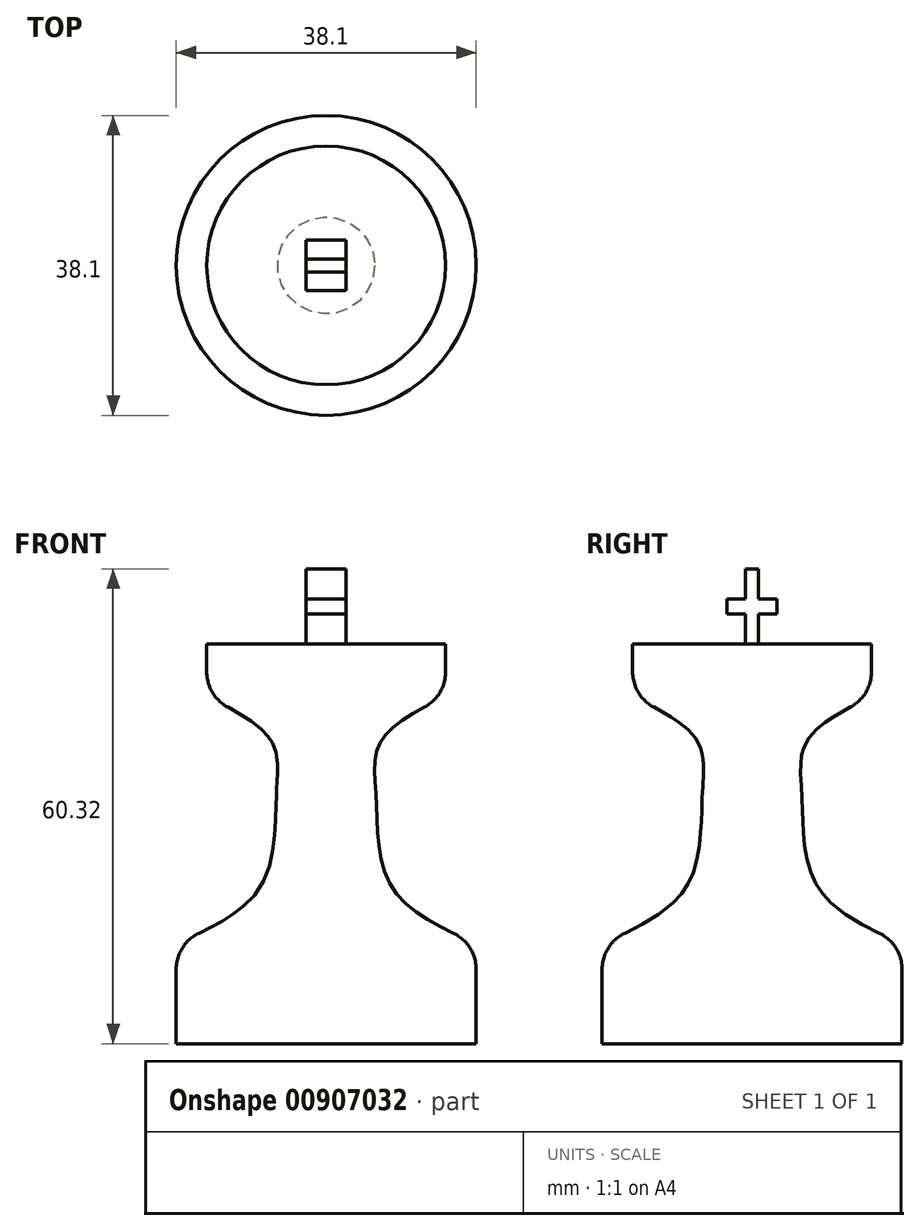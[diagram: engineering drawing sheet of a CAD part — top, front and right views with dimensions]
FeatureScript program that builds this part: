
annotation { "Feature Type Name" : "Feature", "Feature Type Description" : "" }
export const myFeature = defineFeature(function(context is Context, id is Id, definition is map)
    precondition{}
    {
        {
            var Q0;
            Q0=qCreatedBy(makeId("Front.planeOp"),FACE);
            var sketch = newSketch(context, id + "F0", { "sketchPlane" : qUnion([Q0])});
            skLineSegment(sketch, "E0", {"start": v(0, 50.8) * mm, "end": v(0, 0) * mm, "construction": true});
            skLineSegment(sketch, "E1", {"start": v(0, 0) * mm, "end": v(19.05, 0) * mm});
            skLineSegment(sketch, "E2", {"start": v(19.05, 0) * mm, "end": v(19.05, 12.7) * mm});
            skFitSpline(sketch, "E3", {"points": [v(19.05, 12.7) * mm, v(8.22, 20.12) * mm, v(6.33, 31.5) * mm, v(6.96, 38.44) * mm, v(15.17, 44.12) * mm], "startDerivative": vector(-46.7, 21.07) * mm, "endDerivative": vector(41.83, 20.88) * mm});
            skLineSegment(sketch, "E4", {"start": v(15.17, 44.12) * mm, "end": v(15.17, 50.8) * mm});
            skLineSegment(sketch, "E5", {"start": v(15.17, 50.8) * mm, "end": v(0, 50.8) * mm});
            skLineSegment(sketch, "E6", {"start": v(0, 50.8) * mm, "end": v(0, 0) * mm});
            skSolve(sketch);
        }
        {
            var Q0;
            Q0 = qSketchRegion(id + "F0", true);
            var Q1;
            Q1=sQuery(id+"F0.wireOp",EDGE,"E6");
            revolve(context, id + "F1", {"surfaceOperationType" : NewSurfaceOperationType.NEW, "entities" : qUnion([Q0]), "axis" : qUnion([Q1]), "revolveType" : RevolveType.FULL});
        }
        {
            var Q0;
            Q0=makeQuery(id+"F1.opRevolve","SWEPT_EDGE",EDGE,{"disambiguationData":[OSD([sQuery(id+"F0.wireOp",EDGE,"E2"),sQuery(id+"F0.wireOp",EDGE,"E3")])]});
            var Q1;
            Q1=makeQuery(id+"F1.opRevolve","SWEPT_EDGE",EDGE,{"disambiguationData":[OSD([sQuery(id+"F0.wireOp",EDGE,"E3"),sQuery(id+"F0.wireOp",EDGE,"E4")])]});
            fillet(context, id + "F2", {"entities" : qUnion([Q0, Q1]), "radius" : 5.08 * mm, "tangentPropagation" : true, "allowEdgeOverflow" : false});
        }
        {
            var Q0;
            Q0=qCreatedBy(makeId("Right.planeOp"),FACE);
            var sketch = newSketch(context, id + "F3", { "sketchPlane" : qUnion([Q0])});
            skLineSegment(sketch, "E7", {"start": v(0, 50.8) * mm, "end": v(0, 60.32) * mm, "construction": true});
            skLineSegment(sketch, "E8", {"start": v(3.16, 55.56) * mm, "end": v(-3.19, 55.56) * mm, "construction": true});
            skPoint(sketch, "E8.startSnap0", {"position": v(0, 55.56) * mm});
            skLineSegment(sketch, "E9", {"start": v(11.03, 50.8) * mm, "end": v(-11.03, 50.8) * mm, "construction": true});
            skLineSegment(sketch, "E10.bottom", {"start": v(-0.83, 50.8) * mm, "end": v(0.83, 50.8) * mm});
            skLineSegment(sketch, "E10.top", {"start": v(-0.83, 60.32) * mm, "end": v(0.83, 60.32) * mm});
            skLineSegment(sketch, "E10.left", {"start": v(-0.83, 50.8) * mm, "end": v(-0.83, 60.33) * mm});
            skLineSegment(sketch, "E10.right", {"start": v(0.83, 50.8) * mm, "end": v(0.83, 60.33) * mm});
            skLineSegment(sketch, "E11.bottom", {"start": v(-3.19, 54.61) * mm, "end": v(3.19, 54.61) * mm});
            skLineSegment(sketch, "E11.top", {"start": v(-3.19, 56.52) * mm, "end": v(3.19, 56.52) * mm});
            skLineSegment(sketch, "E11.left", {"start": v(-3.19, 54.61) * mm, "end": v(-3.19, 56.52) * mm});
            skLineSegment(sketch, "E11.right", {"start": v(3.19, 54.61) * mm, "end": v(3.19, 56.52) * mm});
            skSolve(sketch);
        }
        {
            var Q0;
            {var subQ5=sQuery(id+"F3.wireOp",EDGE,"E11.right");Q0=makeQuery(id+"F3.imprint","IMPRINT",FACE,{"disambiguationData":[TD([[makeQuery(id+"F3.imprint","IMPRINT",EDGE,{"derivedFrom":subQ5}),1.0]])]});}
            var Q1;
            {var subQ0=sQuery(id+"F3.wireOp",EDGE,"E11.bottom");var subQ1=sQuery(id+"F3.wireOp",EDGE,"E10.left");var subQ2=makeQuery(id+"F3.imprint","INTERSECT",VERTEX,{"derivedFrom":[subQ1,subQ0]});Q1=makeQuery(id+"F3.imprint","IMPRINT",FACE,{"disambiguationData":[TD([[makeQuery(id+"F3.imprint","IMPRINT",EDGE,{"disambiguationData":[TD([[subQ2,-1.0]])],"derivedFrom":subQ1}),-1.0]])]});}
            var Q2;
            {var subQ5=sQuery(id+"F3.wireOp",EDGE,"E11.left");Q2=makeQuery(id+"F3.imprint","IMPRINT",FACE,{"disambiguationData":[TD([[makeQuery(id+"F3.imprint","IMPRINT",EDGE,{"derivedFrom":subQ5}),-1.0]])]});}
            var Q3;
            {var subQ0=sQuery(id+"F3.wireOp",EDGE,"E10.top");Q3=makeQuery(id+"F3.imprint","IMPRINT",FACE,{"disambiguationData":[TD([[makeQuery(id+"F3.imprint","IMPRINT",EDGE,{"derivedFrom":subQ0}),-1.0]])]});}
            var Q4;
            {var subQ0=sQuery(id+"F3.wireOp",EDGE,"E10.bottom");Q4=makeQuery(id+"F3.imprint","IMPRINT",FACE,{"disambiguationData":[TD([[makeQuery(id+"F3.imprint","IMPRINT",EDGE,{"derivedFrom":subQ0}),1.0]])]});}
            extrude(context, id + "F4", {"entities" : qUnion([Q0, Q1, Q2, Q3, Q4]), "operationType" : NewBodyOperationType.ADD, "depth" : 2.54 * mm, "offsetDistance" : 25.4 * mm, "hasSecondDirection" : true, "secondDirectionOppositeDirection" : true, "secondDirectionDepth" : 2.54 * mm});
        }
    });
